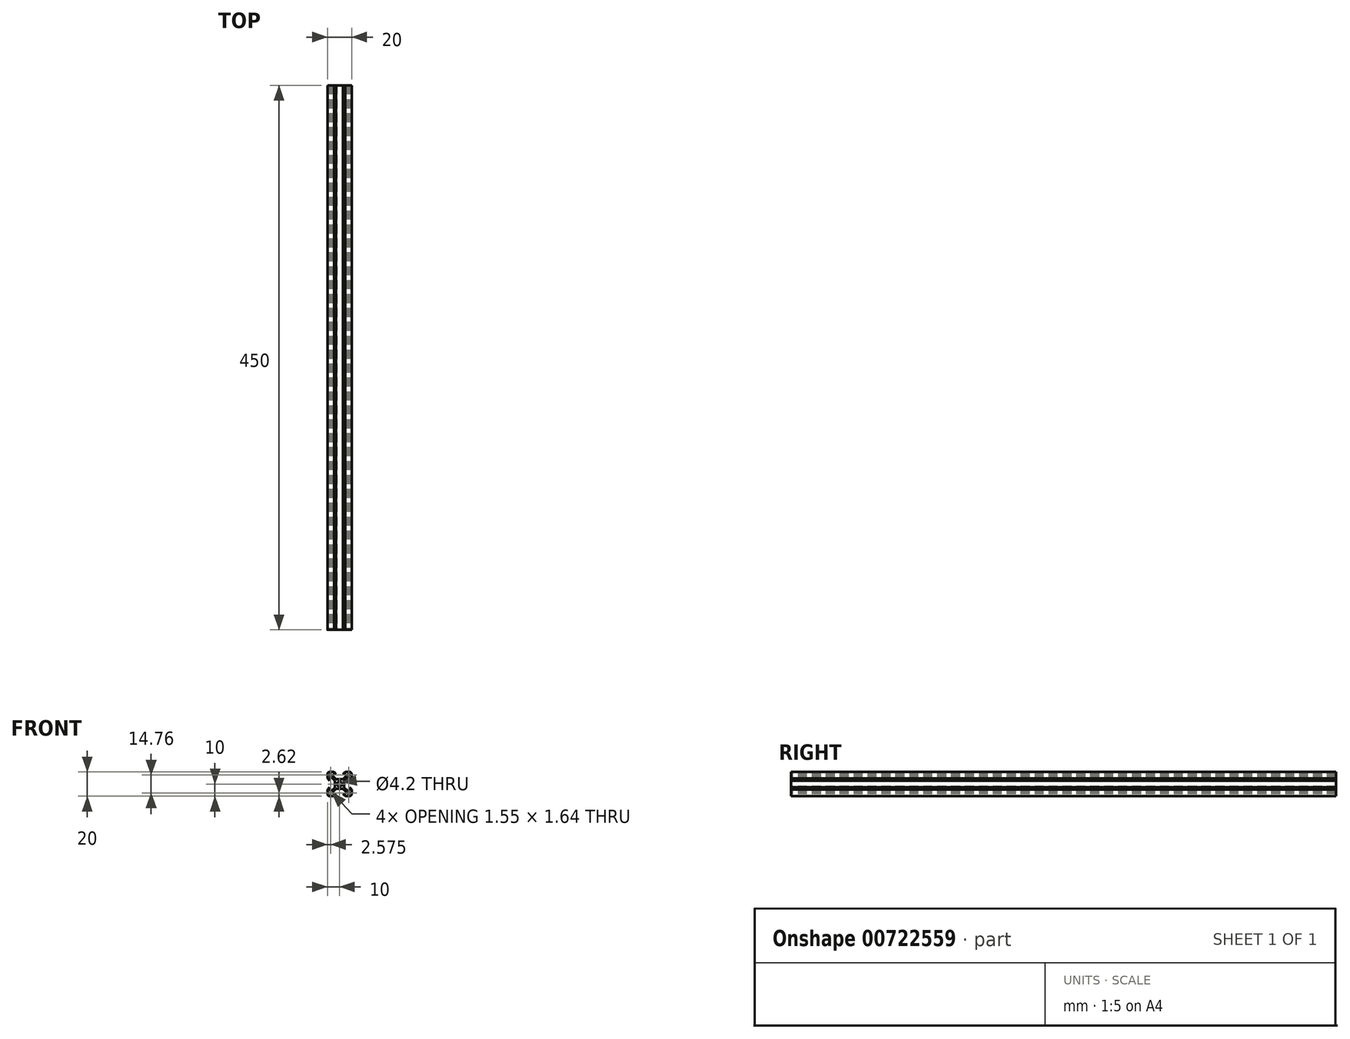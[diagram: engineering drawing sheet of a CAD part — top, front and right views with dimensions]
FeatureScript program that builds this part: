
annotation { "Feature Type Name" : "Feature", "Feature Type Description" : "" }
export const myFeature = defineFeature(function(context is Context, id is Id, definition is map)
    precondition{}
    {
        {
            var Q0;
            Q0=qCreatedBy(makeId("Front.planeOp"),FACE);
            var sketch = newSketch(context, id + "F0", { "sketchPlane" : qUnion([Q0])});
            skLineSegment(sketch, "E0", {"start": v(4.5, 3.44) * mm, "end": v(4.5, 1.8) * mm});
            skLineSegment(sketch, "E1", {"start": v(7.16, 6.1) * mm, "end": v(4.5, 3.44) * mm});
            skLineSegment(sketch, "E2", {"start": v(12.84, 6.1) * mm, "end": v(7.16, 6.1) * mm});
            skLineSegment(sketch, "E3", {"start": v(15.5, 3.44) * mm, "end": v(12.84, 6.1) * mm});
            skLineSegment(sketch, "E4", {"start": v(15.5, 1.8) * mm, "end": v(15.5, 3.44) * mm});
            skLineSegment(sketch, "E5", {"start": v(12.8, 1.8) * mm, "end": v(15.5, 1.8) * mm});
            skLineSegment(sketch, "E6", {"start": v(14.6, 0) * mm, "end": v(12.8, 1.8) * mm});
            skLineSegment(sketch, "E7", {"start": v(18.2, 0) * mm, "end": v(14.6, 0) * mm});
            skArc(sketch, "E8", {"start": v(20, 1.8) * mm, "mid": v(19.47, 0.53) * mm, "end": v(18.2, 0) * mm});
            skLineSegment(sketch, "E9", {"start": v(20, 5.4) * mm, "end": v(20, 1.8) * mm});
            skLineSegment(sketch, "E10", {"start": v(18.2, 7.2) * mm, "end": v(20, 5.4) * mm});
            skLineSegment(sketch, "E11", {"start": v(18.2, 4.5) * mm, "end": v(18.2, 7.2) * mm});
            skLineSegment(sketch, "E12", {"start": v(16.56, 4.5) * mm, "end": v(18.2, 4.5) * mm});
            skLineSegment(sketch, "E13", {"start": v(13.9, 7.16) * mm, "end": v(16.56, 4.5) * mm});
            skLineSegment(sketch, "E14", {"start": v(13.9, 12.84) * mm, "end": v(13.9, 7.16) * mm});
            skLineSegment(sketch, "E15", {"start": v(16.56, 15.5) * mm, "end": v(13.9, 12.84) * mm});
            skLineSegment(sketch, "E16", {"start": v(18.2, 15.5) * mm, "end": v(16.56, 15.5) * mm});
            skLineSegment(sketch, "E17", {"start": v(18.2, 12.8) * mm, "end": v(18.2, 15.5) * mm});
            skLineSegment(sketch, "E18", {"start": v(20, 14.6) * mm, "end": v(18.2, 12.8) * mm});
            skLineSegment(sketch, "E19", {"start": v(20, 18.2) * mm, "end": v(20, 14.6) * mm});
            skArc(sketch, "E20", {"start": v(18.2, 20) * mm, "mid": v(19.47, 19.47) * mm, "end": v(20, 18.2) * mm});
            skLineSegment(sketch, "E21", {"start": v(14.6, 20) * mm, "end": v(18.2, 20) * mm});
            skLineSegment(sketch, "E22", {"start": v(12.8, 18.2) * mm, "end": v(14.6, 20) * mm});
            skLineSegment(sketch, "E23", {"start": v(15.5, 18.2) * mm, "end": v(12.8, 18.2) * mm});
            skLineSegment(sketch, "E24", {"start": v(15.5, 16.56) * mm, "end": v(15.5, 18.2) * mm});
            skLineSegment(sketch, "E25", {"start": v(12.84, 13.9) * mm, "end": v(15.5, 16.56) * mm});
            skLineSegment(sketch, "E26", {"start": v(7.16, 13.9) * mm, "end": v(12.84, 13.9) * mm});
            skLineSegment(sketch, "E27", {"start": v(4.5, 16.56) * mm, "end": v(7.16, 13.9) * mm});
            skLineSegment(sketch, "E28", {"start": v(4.5, 18.2) * mm, "end": v(4.5, 16.56) * mm});
            skLineSegment(sketch, "E29", {"start": v(7.2, 18.2) * mm, "end": v(4.5, 18.2) * mm});
            skLineSegment(sketch, "E30", {"start": v(5.4, 20) * mm, "end": v(7.2, 18.2) * mm});
            skLineSegment(sketch, "E31", {"start": v(1.8, 20) * mm, "end": v(5.4, 20) * mm});
            skArc(sketch, "E32", {"start": v(0, 18.2) * mm, "mid": v(0.53, 19.47) * mm, "end": v(1.8, 20) * mm});
            skLineSegment(sketch, "E33", {"start": v(0, 14.6) * mm, "end": v(0, 18.2) * mm});
            skLineSegment(sketch, "E34", {"start": v(1.8, 12.8) * mm, "end": v(0, 14.6) * mm});
            skLineSegment(sketch, "E35", {"start": v(1.8, 15.5) * mm, "end": v(1.8, 12.8) * mm});
            skLineSegment(sketch, "E36", {"start": v(3.44, 15.5) * mm, "end": v(1.8, 15.5) * mm});
            skLineSegment(sketch, "E37", {"start": v(6.1, 12.84) * mm, "end": v(3.44, 15.5) * mm});
            skLineSegment(sketch, "E38", {"start": v(6.1, 7.16) * mm, "end": v(6.1, 12.84) * mm});
            skLineSegment(sketch, "E39", {"start": v(3.44, 4.5) * mm, "end": v(6.1, 7.16) * mm});
            skLineSegment(sketch, "E40", {"start": v(1.8, 4.5) * mm, "end": v(3.44, 4.5) * mm});
            skLineSegment(sketch, "E41", {"start": v(1.8, 7.2) * mm, "end": v(1.8, 4.5) * mm});
            skLineSegment(sketch, "E42", {"start": v(0, 5.4) * mm, "end": v(1.8, 7.2) * mm});
            skLineSegment(sketch, "E43", {"start": v(0, 1.8) * mm, "end": v(0, 5.4) * mm});
            skArc(sketch, "E44", {"start": v(1.8, 0) * mm, "mid": v(0.53, 0.53) * mm, "end": v(0, 1.8) * mm});
            skLineSegment(sketch, "E45", {"start": v(5.4, 0) * mm, "end": v(1.8, 0) * mm});
            skLineSegment(sketch, "E46", {"start": v(7.2, 1.8) * mm, "end": v(5.4, 0) * mm});
            skLineSegment(sketch, "E47", {"start": v(4.5, 1.8) * mm, "end": v(7.2, 1.8) * mm});
            skCircle(sketch, "E48", {"center": v(10, 10) * mm, "radius": 2.1 * mm});
            skLineSegment(sketch, "E49", {"start": v(16.65, 17.62) * mm, "end": v(17.71, 16.56) * mm});
            skLineSegment(sketch, "E50", {"start": v(16.65, 18.2) * mm, "end": v(16.65, 17.62) * mm});
            skLineSegment(sketch, "E51", {"start": v(18.2, 18.2) * mm, "end": v(16.65, 18.2) * mm});
            skLineSegment(sketch, "E52", {"start": v(18.2, 16.56) * mm, "end": v(18.2, 18.2) * mm});
            skLineSegment(sketch, "E53", {"start": v(17.71, 16.56) * mm, "end": v(18.2, 16.56) * mm});
            skLineSegment(sketch, "E54", {"start": v(1.8, 18.2) * mm, "end": v(1.8, 16.56) * mm});
            skLineSegment(sketch, "E55", {"start": v(3.35, 18.2) * mm, "end": v(1.8, 18.2) * mm});
            skLineSegment(sketch, "E56", {"start": v(3.35, 17.62) * mm, "end": v(3.35, 18.2) * mm});
            skLineSegment(sketch, "E57", {"start": v(2.29, 16.56) * mm, "end": v(3.35, 17.62) * mm});
            skLineSegment(sketch, "E58", {"start": v(1.8, 16.56) * mm, "end": v(2.29, 16.56) * mm});
            skLineSegment(sketch, "E59", {"start": v(18.2, 1.8) * mm, "end": v(18.2, 3.44) * mm});
            skLineSegment(sketch, "E60", {"start": v(16.65, 1.8) * mm, "end": v(18.2, 1.8) * mm});
            skLineSegment(sketch, "E61", {"start": v(16.65, 2.38) * mm, "end": v(16.65, 1.8) * mm});
            skLineSegment(sketch, "E62", {"start": v(17.71, 3.44) * mm, "end": v(16.65, 2.38) * mm});
            skLineSegment(sketch, "E63", {"start": v(18.2, 3.44) * mm, "end": v(17.71, 3.44) * mm});
            skLineSegment(sketch, "E64", {"start": v(3.35, 2.38) * mm, "end": v(2.29, 3.44) * mm});
            skLineSegment(sketch, "E65", {"start": v(3.35, 1.8) * mm, "end": v(3.35, 2.38) * mm});
            skLineSegment(sketch, "E66", {"start": v(1.8, 1.8) * mm, "end": v(3.35, 1.8) * mm});
            skLineSegment(sketch, "E67", {"start": v(1.8, 3.44) * mm, "end": v(1.8, 1.8) * mm});
            skLineSegment(sketch, "E68", {"start": v(2.29, 3.44) * mm, "end": v(1.8, 3.44) * mm});
            skSolve(sketch);
        }
        {
            var Q0;
            Q0=makeQuery(id+"F0.imprint","IMPRINT",FACE,{"disambiguationData":[TD([[makeQuery(id+"F0.imprint","IMPRINT",EDGE,{"derivedFrom":sQuery(id+"F0.wireOp",EDGE,"E0")}),-1.0]])]});
            extrude(context, id + "F1", {"entities" : qUnion([Q0]), "depth" : -450 * mm, "offsetDistance" : 25 * mm});
        }
    });
